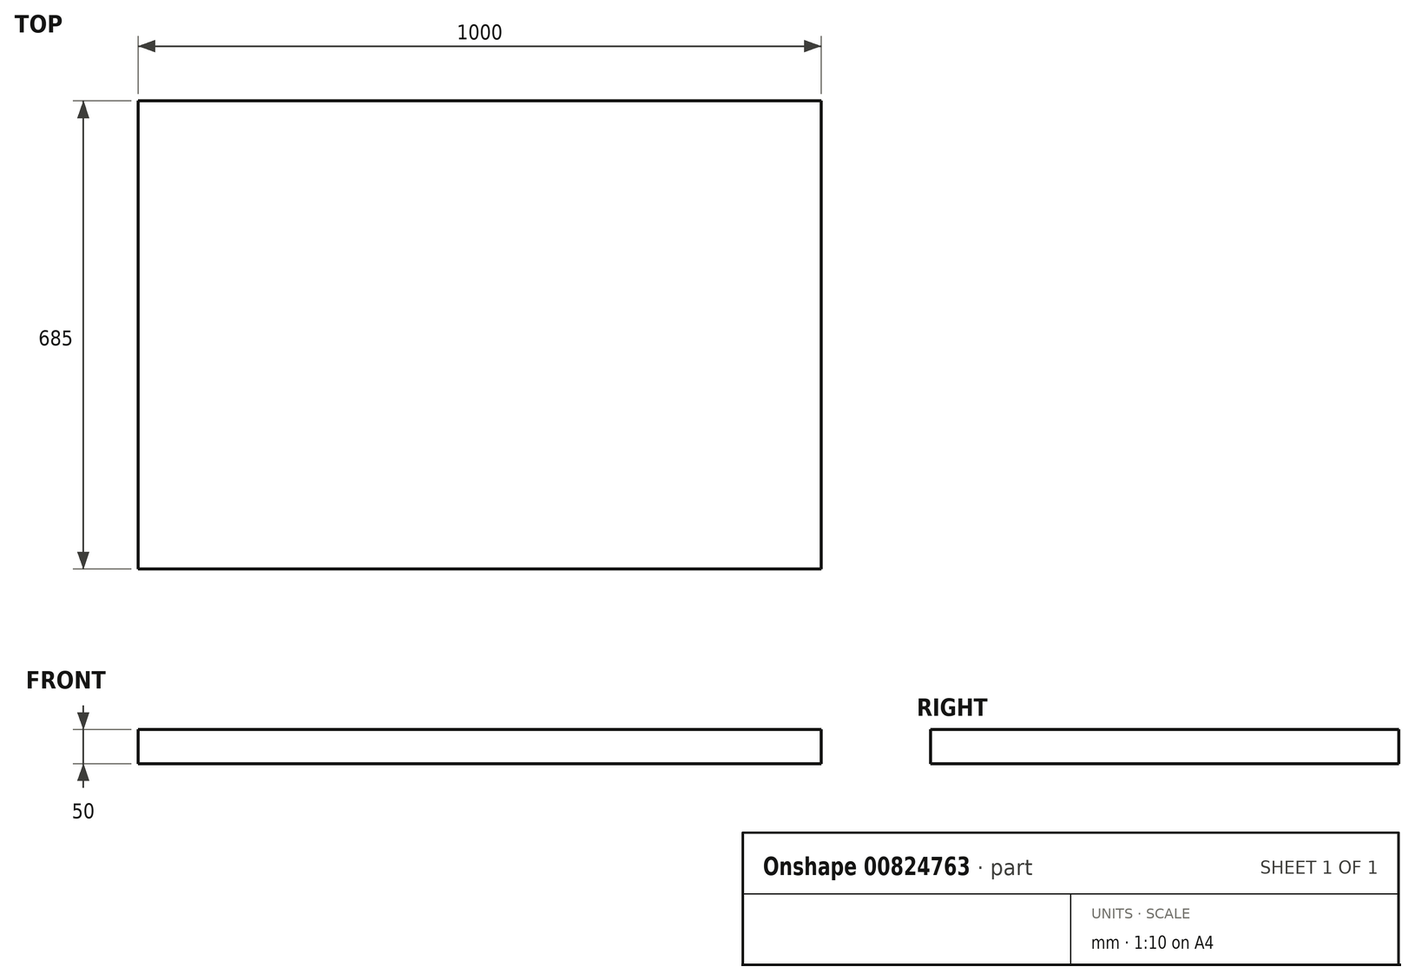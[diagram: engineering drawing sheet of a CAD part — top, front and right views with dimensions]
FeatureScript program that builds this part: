
annotation { "Feature Type Name" : "Feature", "Feature Type Description" : "" }
export const myFeature = defineFeature(function(context is Context, id is Id, definition is map)
    precondition{}
    {
        {
            var Q0;
            Q0=qCreatedBy(makeId("Top.planeOp"),FACE);
            var sketch = newSketch(context, id + "F0", { "sketchPlane" : qUnion([Q0])});
            skLineSegment(sketch, "E0.bottom", {"start": v(-440.37, -347.61) * mm, "end": v(559.63, -347.61) * mm});
            skLineSegment(sketch, "E0.top", {"start": v(-440.37, 337.39) * mm, "end": v(559.63, 337.39) * mm});
            skLineSegment(sketch, "E0.left", {"start": v(-440.37, -347.61) * mm, "end": v(-440.37, 337.39) * mm});
            skLineSegment(sketch, "E0.right", {"start": v(559.63, -347.61) * mm, "end": v(559.63, 337.39) * mm});
            skSolve(sketch);
        }
        {
            var Q0;
            Q0=makeQuery(id+"F0.imprint","IMPRINT",FACE,{"disambiguationData":[TD([[makeQuery(id+"F0.imprint","IMPRINT",EDGE,{"derivedFrom":sQuery(id+"F0.wireOp",EDGE,"E0.bottom")}),1.0]])]});
            extrude(context, id + "F1", {"entities" : qUnion([Q0]), "depth" : 50 * mm, "offsetDistance" : 25 * mm});
        }
        {
            var Q0;
            Q0=makeQuery(id+"F1.opExtrude","SWEPT_FACE",FACE,{"disambiguationData":[OSD([sQuery(id+"F0.wireOp",EDGE,"E0.bottom")])]});
            var sketch = newSketch(context, id + "F2", { "sketchPlane" : qUnion([Q0])});
            skLineSegment(sketch, "E1", {"start": v(-190.37, 50) * mm, "end": v(-190.37, 24) * mm});
            skLineSegment(sketch, "E2", {"start": v(-190.37, 24) * mm, "end": v(102.63, 24) * mm});
            skCircle(sketch, "E3", {"center": v(-190.37, 24) * mm, "radius": 5 * mm});
            skCircle(sketch, "E4", {"center": v(102.63, 24) * mm, "radius": 5 * mm});
            skLineSegment(sketch, "E5", {"start": v(-190.37, 24) * mm, "end": v(-440.37, 24) * mm});
            skSolve(sketch);
        }
        {
            var Q0;
            Q0=makeQuery(id+"F1.opExtrude","SWEPT_FACE",FACE,{"disambiguationData":[OSD([sQuery(id+"F0.wireOp",EDGE,"E0.top")])]});
            var sketch = newSketch(context, id + "F3", { "sketchPlane" : qUnion([Q0])});
            skLineSegment(sketch, "E6", {"start": v(440.37, 50) * mm, "end": v(440.37, 25) * mm});
            skLineSegment(sketch, "E7", {"start": v(440.37, 25) * mm, "end": v(190.37, 25) * mm});
            skLineSegment(sketch, "E8", {"start": v(190.37, 25) * mm, "end": v(-102.63, 25) * mm});
            skCircle(sketch, "E9", {"center": v(-102.63, 25) * mm, "radius": 5 * mm});
            skCircle(sketch, "E10", {"center": v(190.37, 25) * mm, "radius": 5 * mm});
            skSolve(sketch);
        }
    });
